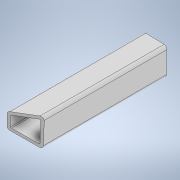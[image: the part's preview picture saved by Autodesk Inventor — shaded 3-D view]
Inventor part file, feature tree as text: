
AUTODESK INVENTOR PART (.ipt)
format: ipt  version: 2021 (Build 250183000, 183)  size: 143,872 bytes
history: native  units: mm
features: extrude x2, sketch x2, fillet x1, projected_geometry x1
ambient origin geometry x8: Origin, YZ Plane, XZ Plane, XY Plane, X Axis, Y Axis, Z Axis, Center Point
bodies: Volumenkörper1 (feature_tree)
feature tree (6):
  extrude  "Extrusion1"  Depth=12.0mm
  extrude  "Extrusion2"  Depth=1.0mm
  fillet  "Rundung1"  Radius=17.627825mm
  sketch  "Skizze1"  dims[d0=26.0mm d1=12.0mm]
  sketch  "Skizze3"  dims[d3=26.0mm d4=24.0mm d7=17.627825mm d8=13.58315mm d9=3.0mm d10=3.0mm d11=3.0mm d12=3.0mm d13=150.0mm d14=0.0mm d19=13.613568mm d20=12.915436mm d21=149.0mm d22=0.0mm d23=3.0mm d24=1.0mm d25=150.0mm]
  projected_geometry  "Projizierte Kontur1"
